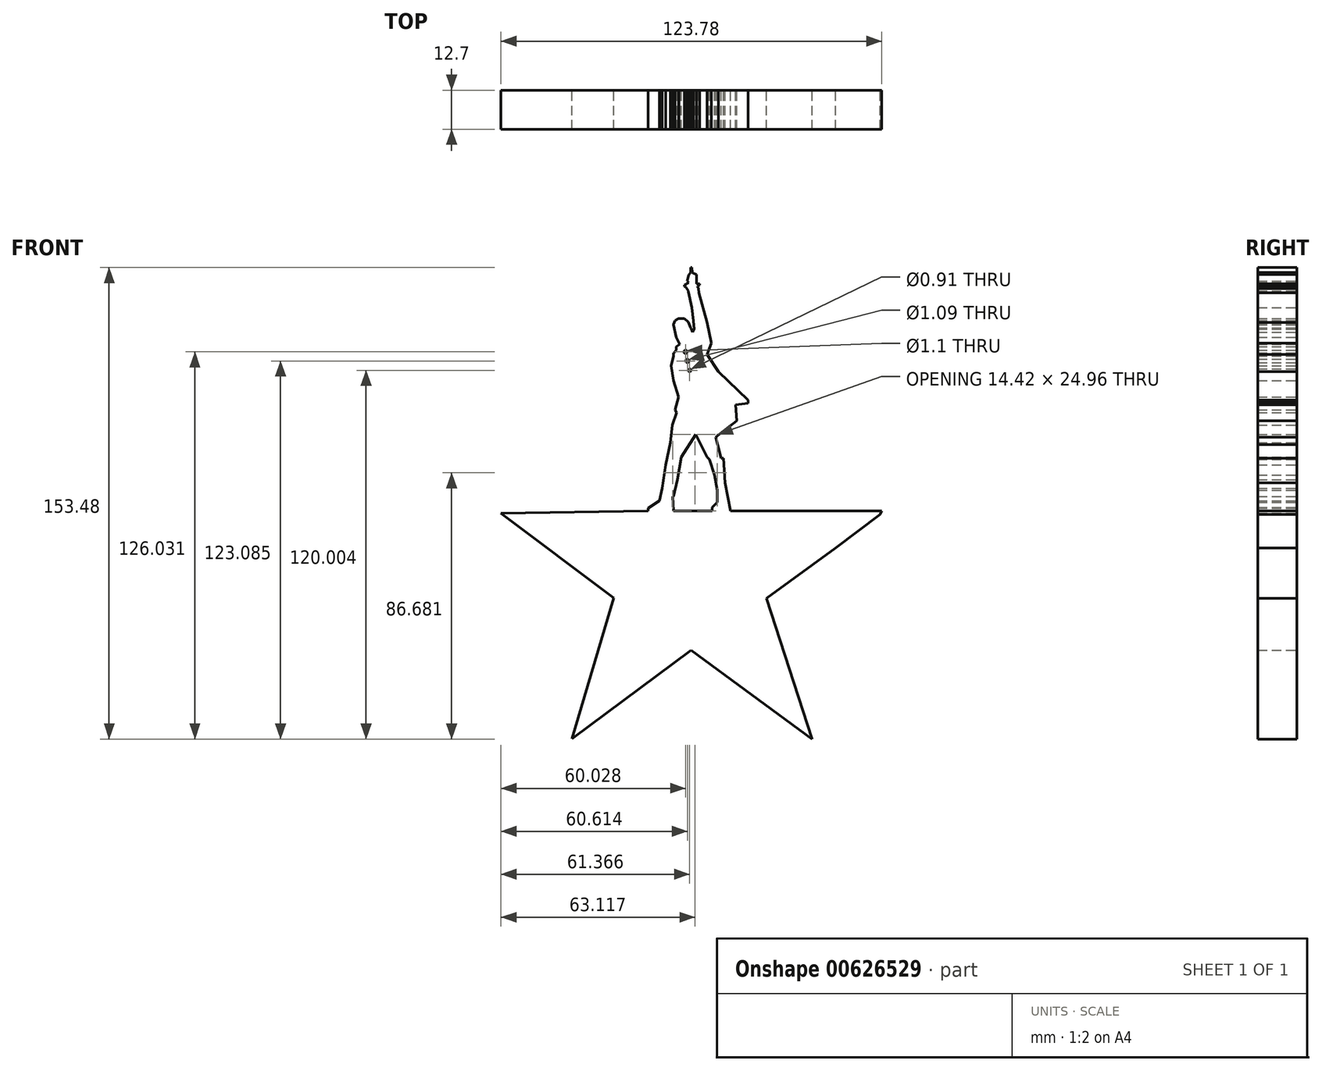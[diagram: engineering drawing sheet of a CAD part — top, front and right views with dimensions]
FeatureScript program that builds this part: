
annotation { "Feature Type Name" : "Feature", "Feature Type Description" : "" }
export const myFeature = defineFeature(function(context is Context, id is Id, definition is map)
    precondition{}
    {
        {
            var Q0;
            Q0=qCreatedBy(makeId("Front.planeOp"),FACE);
            var sketch = newSketch(context, id + "F0", { "sketchPlane" : qUnion([Q0])});
            skLineSegment(sketch, "E0", {"start": v(-0.76, -36.7) * mm, "end": v(35.8, -63.55) * mm});
            skLineSegment(sketch, "E1", {"start": v(35.8, -63.55) * mm, "end": v(38.6, -65.6) * mm});
            skLineSegment(sketch, "E2", {"start": v(38.6, -65.6) * mm, "end": v(31.08, -42.4) * mm});
            skLineSegment(sketch, "E3", {"start": v(31.08, -42.4) * mm, "end": v(24.74, -22.88) * mm});
            skLineSegment(sketch, "E4", {"start": v(24.74, -22.88) * mm, "end": v(23.72, -19.76) * mm});
            skLineSegment(sketch, "E5", {"start": v(23.72, -19.76) * mm, "end": v(46.14, -3.46) * mm});
            skLineSegment(sketch, "E6", {"start": v(46.14, -3.46) * mm, "end": v(60.68, 7.5) * mm});
            skLineSegment(sketch, "E7", {"start": v(11.96, 8.6) * mm, "end": v(61.15, 8.6) * mm});
            skLineSegment(sketch, "E8", {"start": v(61.15, 8.6) * mm, "end": v(60.68, 7.5) * mm});
            skLineSegment(sketch, "E9", {"start": v(7.7, 11.4) * mm, "end": v(6, 9.8) * mm});
            skLineSegment(sketch, "E10", {"start": v(6, 9.8) * mm, "end": v(6, 8.6) * mm});
            skLineSegment(sketch, "E11", {"start": v(6, 8.6) * mm, "end": v(-6.57, 8.6) * mm});
            skLineSegment(sketch, "E12", {"start": v(-9.9, 9.16) * mm, "end": v(-9.9, 8.6) * mm});
            skLineSegment(sketch, "E13", {"start": v(-9.83, 8.39) * mm, "end": v(-6.57, 8.39) * mm});
            skLineSegment(sketch, "E14", {"start": v(-6.72, 13.37) * mm, "end": v(-6.57, 8.6) * mm});
            skLineSegment(sketch, "E15", {"start": v(-14.84, 9.77) * mm, "end": v(-14.84, 8.6) * mm});
            skLineSegment(sketch, "E16", {"start": v(-14.84, 9.52) * mm, "end": v(-11.1, 11.93) * mm});
            skLineSegment(sketch, "E17", {"start": v(-11.1, 11.93) * mm, "end": v(-10.15, 16.05) * mm});
            skLineSegment(sketch, "E18", {"start": v(-10.15, 16.05) * mm, "end": v(-9.08, 23.67) * mm});
            skLineSegment(sketch, "E19", {"start": v(-9.08, 23.67) * mm, "end": v(-7.56, 30.83) * mm});
            skLineSegment(sketch, "E20", {"start": v(-7.56, 30.83) * mm, "end": v(-6.89, 36.54) * mm});
            skLineSegment(sketch, "E21", {"start": v(-6.89, 36.54) * mm, "end": v(-5.47, 40.61) * mm});
            skLineSegment(sketch, "E22", {"start": v(-5.47, 40.61) * mm, "end": v(-6.08, 41.56) * mm});
            skLineSegment(sketch, "E23", {"start": v(-6.08, 41.56) * mm, "end": v(-4.93, 45.7) * mm});
            skLineSegment(sketch, "E24", {"start": v(-4.93, 45.7) * mm, "end": v(-6.57, 51.12) * mm});
            skLineSegment(sketch, "E25", {"start": v(-6.57, 51.12) * mm, "end": v(-7.3, 55.93) * mm});
            skCircle(sketch, "E26", {"center": v(-1.26, 54.4) * mm, "radius": 0.45 * mm});
            skCircle(sketch, "E27", {"center": v(-2.02, 57.48) * mm, "radius": 0.54 * mm});
            skCircle(sketch, "E28", {"center": v(-2.6, 60.42) * mm, "radius": 0.55 * mm});
            skLineSegment(sketch, "E29", {"start": v(-7.3, 55.93) * mm, "end": v(-6.48, 59.02) * mm});
            skLineSegment(sketch, "E30", {"start": v(-6.48, 59.02) * mm, "end": v(-6.48, 60.05) * mm});
            skLineSegment(sketch, "E31", {"start": v(-6.42, 60.1) * mm, "end": v(-5.6, 60.95) * mm});
            skLineSegment(sketch, "E32", {"start": v(-5.6, 60.95) * mm, "end": v(-5.6, 61.94) * mm});
            skLineSegment(sketch, "E33", {"start": v(-5.6, 62.06) * mm, "end": v(-4.44, 62.87) * mm});
            skLineSegment(sketch, "E34", {"start": v(-5.6, 65.16) * mm, "end": v(-4.44, 62.87) * mm});
            skLineSegment(sketch, "E35", {"start": v(-6.48, 69.2) * mm, "end": v(-5.6, 65.16) * mm});
            skLineSegment(sketch, "E36", {"start": v(-6.48, 69.33) * mm, "end": v(-6, 70.63) * mm});
            skLineSegment(sketch, "E37", {"start": v(-6, 70.63) * mm, "end": v(-4.88, 71.2) * mm});
            skLineSegment(sketch, "E38", {"start": v(-4.77, 71.2) * mm, "end": v(-3, 71.2) * mm});
            skLineSegment(sketch, "E39", {"start": v(-3, 71.2) * mm, "end": v(-1.67, 70.18) * mm});
            skLineSegment(sketch, "E40", {"start": v(-1.67, 70.18) * mm, "end": v(-0.92, 68.24) * mm});
            skLineSegment(sketch, "E41", {"start": v(-0.87, 68.07) * mm, "end": v(-0.25, 66.84) * mm});
            skLineSegment(sketch, "E42", {"start": v(-0.92, 68.24) * mm, "end": v(-0.87, 68.07) * mm});
            skLineSegment(sketch, "E43", {"start": v(0, 70.5) * mm, "end": v(0.24, 67.85) * mm});
            skLineSegment(sketch, "E44", {"start": v(0.24, 67.85) * mm, "end": v(-0.25, 66.84) * mm});
            skLineSegment(sketch, "E45", {"start": v(-0.51, 74.77) * mm, "end": v(0, 70.5) * mm});
            skLineSegment(sketch, "E46", {"start": v(-1.67, 80) * mm, "end": v(-0.51, 74.77) * mm});
            skLineSegment(sketch, "E47", {"start": v(-1.67, 80.23) * mm, "end": v(-2.5, 81.42) * mm});
            skLineSegment(sketch, "E48", {"start": v(-1.67, 80.23) * mm, "end": v(-1.67, 80) * mm});
            skLineSegment(sketch, "E49", {"start": v(-2.5, 81.55) * mm, "end": v(-3, 81.7) * mm});
            skLineSegment(sketch, "E50", {"start": v(-2.92, 82.18) * mm, "end": v(-3, 81.7) * mm});
            skLineSegment(sketch, "E51", {"start": v(-2.92, 82.18) * mm, "end": v(-1.53, 82.94) * mm});
            skLineSegment(sketch, "E52", {"start": v(-2.04, 83.48) * mm, "end": v(-1.53, 82.94) * mm});
            skLineSegment(sketch, "E53", {"start": v(-1.53, 85.42) * mm, "end": v(-2.04, 83.48) * mm});
            skLineSegment(sketch, "E54", {"start": v(-1.53, 85.42) * mm, "end": v(-0.92, 86.24) * mm});
            skLineSegment(sketch, "E55", {"start": v(-0.89, 87.87) * mm, "end": v(-0.92, 86.24) * mm});
            skLineSegment(sketch, "E56", {"start": v(-0.89, 87.87) * mm, "end": v(-0.57, 87.86) * mm});
            skLineSegment(sketch, "E57", {"start": v(-0.57, 87.86) * mm, "end": v(-0.45, 86.24) * mm});
            skLineSegment(sketch, "E58", {"start": v(-0.45, 86.24) * mm, "end": v(-0.21, 85.99) * mm});
            skLineSegment(sketch, "E59", {"start": v(-0.21, 85.97) * mm, "end": v(0, 85.97) * mm});
            skLineSegment(sketch, "E60", {"start": v(0, 85.97) * mm, "end": v(0.98, 85.61) * mm});
            skLineSegment(sketch, "E61", {"start": v(0.98, 85.61) * mm, "end": v(0.98, 82.6) * mm});
            skLineSegment(sketch, "E62", {"start": v(0.98, 82.6) * mm, "end": v(2.03, 82.6) * mm});
            skLineSegment(sketch, "E63", {"start": v(2.03, 82.6) * mm, "end": v(2.03, 82.16) * mm});
            skLineSegment(sketch, "E64", {"start": v(2, 82.14) * mm, "end": v(1.21, 81.75) * mm});
            skLineSegment(sketch, "E65", {"start": v(1.21, 81.75) * mm, "end": v(1.56, 81.06) * mm});
            skLineSegment(sketch, "E66", {"start": v(1.56, 81.06) * mm, "end": v(1.73, 79.68) * mm});
            skLineSegment(sketch, "E67", {"start": v(1.73, 79.68) * mm, "end": v(4.37, 69.92) * mm});
            skLineSegment(sketch, "E68", {"start": v(4.37, 69.92) * mm, "end": v(5.84, 63.28) * mm});
            skLineSegment(sketch, "E69", {"start": v(5.84, 63.28) * mm, "end": v(4.37, 59.56) * mm});
            skLineSegment(sketch, "E70", {"start": v(4.37, 59.56) * mm, "end": v(8.13, 54.04) * mm});
            skLineSegment(sketch, "E71", {"start": v(8.13, 54.04) * mm, "end": v(17.68, 44.72) * mm});
            skLineSegment(sketch, "E72", {"start": v(13.72, 43.18) * mm, "end": v(17.78, 43.7) * mm});
            skLineSegment(sketch, "E73", {"start": v(17.68, 44.57) * mm, "end": v(17.78, 43.7) * mm});
            skLineSegment(sketch, "E74", {"start": v(13.72, 43.18) * mm, "end": v(14, 38.02) * mm});
            skLineSegment(sketch, "E75", {"start": v(7.23, 32.7) * mm, "end": v(14, 38.02) * mm});
            skLineSegment(sketch, "E76", {"start": v(7.23, 32.7) * mm, "end": v(7.78, 30.23) * mm});
            skLineSegment(sketch, "E77", {"start": v(7.78, 30.23) * mm, "end": v(8.97, 25.81) * mm});
            skLineSegment(sketch, "E78", {"start": v(8.8, 25.82) * mm, "end": v(9.67, 25.81) * mm});
            skLineSegment(sketch, "E79", {"start": v(9.67, 25.81) * mm, "end": v(10.22, 17.82) * mm});
            skLineSegment(sketch, "E80", {"start": v(10.22, 17.82) * mm, "end": v(11.96, 8.6) * mm});
            skLineSegment(sketch, "E81", {"start": v(7.7, 11.4) * mm, "end": v(7.7, 15.4) * mm});
            skLineSegment(sketch, "E82", {"start": v(7.7, 15.4) * mm, "end": v(6.76, 20.36) * mm});
            skLineSegment(sketch, "E83", {"start": v(6.76, 20.36) * mm, "end": v(5.12, 25.46) * mm});
            skLineSegment(sketch, "E84", {"start": v(5.12, 25.46) * mm, "end": v(4.54, 26.1) * mm});
            skLineSegment(sketch, "E85", {"start": v(4.45, 26.15) * mm, "end": v(0.68, 33.55) * mm});
            skLineSegment(sketch, "E86", {"start": v(0.68, 33.55) * mm, "end": v(-3.97, 26.18) * mm});
            skLineSegment(sketch, "E87", {"start": v(-3.97, 26.18) * mm, "end": v(-5.24, 18.82) * mm});
            skLineSegment(sketch, "E88", {"start": v(-6.48, 13.37) * mm, "end": v(-5.24, 18.82) * mm});
            skLineSegment(sketch, "E89", {"start": v(-14.84, 8.6) * mm, "end": v(-9.83, 8.39) * mm});
            skLineSegment(sketch, "E90", {"start": v(-0.76, -36.7) * mm, "end": v(-39.53, -65.54) * mm});
            skLineSegment(sketch, "E91", {"start": v(-39.53, -65.54) * mm, "end": v(-25.93, -19.62) * mm});
            skLineSegment(sketch, "E92", {"start": v(-25.93, -19.62) * mm, "end": v(-62.63, 7.85) * mm});
            skLineSegment(sketch, "E93", {"start": v(-63.5, 8.72) * mm, "end": v(-62.63, 7.85) * mm});
            skLineSegment(sketch, "E94", {"start": v(-62.63, 7.85) * mm, "end": v(-14.84, 8.6) * mm});
            skLineSegment(sketch, "E95", {"start": v(6, 8.6) * mm, "end": v(11.96, 8.6) * mm});
            skLineSegment(sketch, "E96", {"start": v(4.45, 26.15) * mm, "end": v(4.54, 26.1) * mm});
            skLineSegment(sketch, "E97", {"start": v(17.68, 44.72) * mm, "end": v(17.68, 44.57) * mm});
            skLineSegment(sketch, "E98", {"start": v(-2.5, 81.42) * mm, "end": v(-2.5, 81.55) * mm});
            skLineSegment(sketch, "E99", {"start": v(-4.88, 71.2) * mm, "end": v(-4.77, 71.2) * mm});
            skLineSegment(sketch, "E100", {"start": v(-6.48, 69.33) * mm, "end": v(-6.48, 69.2) * mm});
            skLineSegment(sketch, "E101", {"start": v(-5.6, 62.06) * mm, "end": v(-5.6, 61.94) * mm});
            skLineSegment(sketch, "E102", {"start": v(-6.48, 60.05) * mm, "end": v(-6.42, 60.1) * mm});
            skLineSegment(sketch, "E103", {"start": v(-0.21, 85.99) * mm, "end": v(-0.21, 85.97) * mm});
            skLineSegment(sketch, "E104", {"start": v(2, 82.14) * mm, "end": v(2.03, 82.16) * mm});
            skLineSegment(sketch, "E105", {"start": v(-6.72, 13.37) * mm, "end": v(-6.48, 13.37) * mm});
            skSolve(sketch);
        }
        {
            var Q0;
            Q0 = qSketchRegion(id + "F0", true);
            extrude(context, id + "F1", {"entities" : qUnion([Q0]), "depth" : 12.7 * mm, "offsetDistance" : 25.4 * mm});
        }
    });
